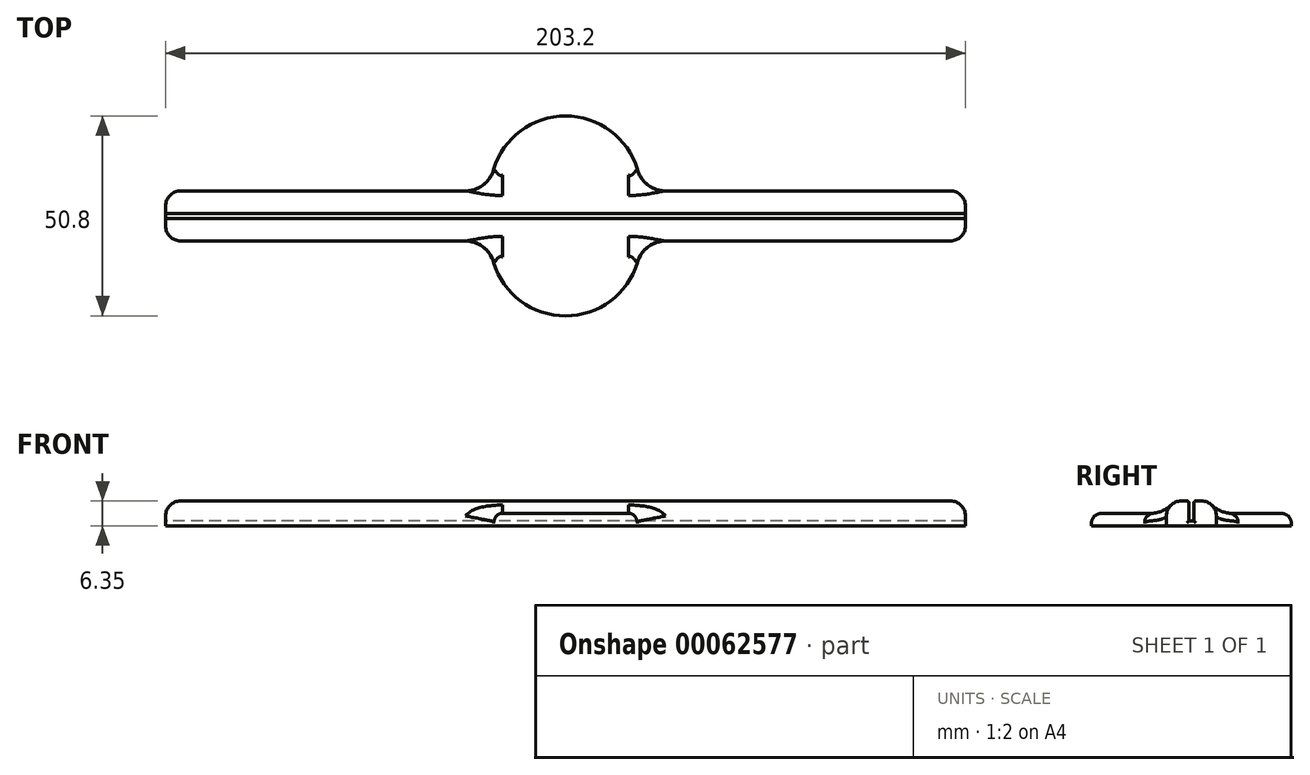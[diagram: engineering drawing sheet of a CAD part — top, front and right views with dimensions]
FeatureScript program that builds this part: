
annotation { "Feature Type Name" : "Feature", "Feature Type Description" : "" }
export const myFeature = defineFeature(function(context is Context, id is Id, definition is map)
    precondition{}
    {
        {
            var Q0;
            Q0=qCreatedBy(makeId("Right.planeOp"),FACE);
            var sketch = newSketch(context, id + "F0", { "sketchPlane" : qUnion([Q0])});
            skPoint(sketch, "E0.visualSharp", {"position": v(5.72, 1.27) * mm});
            skPoint(sketch, "E1.visualSharp", {"position": v(6.99, 1.27) * mm});
            skPoint(sketch, "E2.visualSharp", {"position": v(0, 6.35) * mm});
            skPoint(sketch, "E3.visualSharp", {"position": v(12.7, 6.35) * mm});
            skPoint(sketch, "E4.visualSharp", {"position": v(5.72, 6.35) * mm});
            skPoint(sketch, "E5.visualSharp", {"position": v(6.99, 6.35) * mm});
            skLineSegment(sketch, "E6", {"start": v(12.7, 0) * mm, "end": v(12.7, 6.35) * mm});
            skLineSegment(sketch, "E7", {"start": v(6.99, 6.35) * mm, "end": v(12.7, 6.35) * mm});
            skLineSegment(sketch, "E8", {"start": v(5.72, 6.35) * mm, "end": v(0, 6.35) * mm});
            skLineSegment(sketch, "E9", {"start": v(5.72, 6.35) * mm, "end": v(5.72, 1.27) * mm});
            skLineSegment(sketch, "E10", {"start": v(6.99, 6.35) * mm, "end": v(6.99, 1.27) * mm});
            skLineSegment(sketch, "E11", {"start": v(6.99, 1.27) * mm, "end": v(5.72, 1.27) * mm});
            skLineSegment(sketch, "E12", {"start": v(12.7, 0) * mm, "end": v(0, 0) * mm});
            skLineSegment(sketch, "E13", {"start": v(0, 0) * mm, "end": v(0, 6.35) * mm});
            skSolve(sketch);
        }
        {
            var Q0;
            Q0=makeQuery(id+"F0.imprint","IMPRINT",FACE,{"disambiguationData":[TD([[makeQuery(id+"F0.imprint","IMPRINT",EDGE,{"derivedFrom":sQuery(id+"F0.wireOp",EDGE,"991Wu4Bv-dtFn-WpcZ-A5Xh-EiTTtVhIbmSV")}),1.0]])]});
            var Q1;
            Q1=makeQuery(id+"F0.imprint","IMPRINT",FACE,{"disambiguationData":[TD([[makeQuery(id+"F0.imprint","IMPRINT",EDGE,{"derivedFrom":sQuery(id+"F0.wireOp",EDGE,"E6")}),1.0]])]});
            extrude(context, id + "F1", {"entities" : qUnion([Q0, Q1]), "depth" : 203.2 * mm});
        }
        {
            var Q0;
            Q0=qCreatedBy(makeId("Top.planeOp"),FACE);
            var sketch = newSketch(context, id + "F2", { "sketchPlane" : qUnion([Q0])});
            skArc(sketch, "E14", {"start": v(83.26, 5.16) * mm, "mid": v(101.6, -19.05) * mm, "end": v(119.94, 5.16) * mm});
            skArc(sketch, "E15", {"start": v(119.94, 7.54) * mm, "mid": v(101.6, 31.75) * mm, "end": v(83.26, 7.54) * mm});
            skLineSegment(sketch, "E16", {"start": v(83.26, 5.16) * mm, "end": v(119.94, 5.16) * mm});
            skLineSegment(sketch, "E17", {"start": v(119.94, 7.54) * mm, "end": v(83.26, 7.54) * mm});
            skSolve(sketch);
        }
        {
            var Q0;
            Q0=makeQuery(id+"F2.imprint","IMPRINT",FACE,{"disambiguationData":[TD([[makeQuery(id+"F2.imprint","IMPRINT",EDGE,{"derivedFrom":sQuery(id+"F2.wireOp",EDGE,"E15")}),1.0]])]});
            var Q1;
            Q1=makeQuery(id+"F2.imprint","IMPRINT",FACE,{"disambiguationData":[TD([[makeQuery(id+"F2.imprint","IMPRINT",EDGE,{"derivedFrom":sQuery(id+"F2.wireOp",EDGE,"E14")}),1.0]])]});
            var Q2;
            Q2=makeQuery(id+"F2.imprint","IMPRINT",FACE,{"disambiguationData":[TD([[makeQuery(id+"F2.imprint","IMPRINT",EDGE,{"derivedFrom":sQuery(id+"F2.wireOp",EDGE,"aa7551ad-62cc-4337-8cd2-00c71349cac6")}),1.0]])]});
            var Q3;
            Q3=makeQuery(id+"F2.imprint","IMPRINT",FACE,{"disambiguationData":[TD([[makeQuery(id+"F2.imprint","IMPRINT",EDGE,{"derivedFrom":sQuery(id+"F2.wireOp",EDGE,"730a3766-1bab-460e-ae77-063c695d67be")}),1.0]])]});
            extrude(context, id + "F3", {"entities" : qUnion([Q0, Q1, Q2, Q3]), "operationType" : NewBodyOperationType.ADD, "depth" : 3.17 * mm});
        }
        {
            var Q0;
            Q0=makeQuery(id+"F1.opExtrude","SWEPT_EDGE",EDGE,{"disambiguationData":[OSD([sQuery(id+"F0.wireOp",EDGE,"E6"),sQuery(id+"F0.wireOp",EDGE,"E7")])]});
            var Q1;
            Q1=makeQuery(id+"F1.opExtrude","SWEPT_EDGE",EDGE,{"disambiguationData":[OSD([sQuery(id+"F0.wireOp",EDGE,"E8"),sQuery(id+"F0.wireOp",EDGE,"E13")])]});
            fillet(context, id + "F4", {"entities" : qUnion([Q0, Q1]), "radius" : 3.8 * mm, "tangentPropagation" : true, "allowEdgeOverflow" : false});
        }
        {
            var Q0;
            {var subQ0=sQuery(id+"F0.wireOp",EDGE,"E7");var subQ1=sQuery(id+"F0.wireOp",EDGE,"E6");Q0=makeQuery(id+"F4.opFillet","BLEND_EDGE",EDGE,{"blendedFrom":[makeQuery(id+"F1.opExtrude","SWEPT_EDGE",EDGE,{"disambiguationData":[OSD([subQ1,subQ0])]}),makeQuery(id+"F1.opExtrude","CAP_FACE",FACE,{"disambiguationData":[OSD([subQ1,subQ0,sQuery(id+"F0.wireOp",EDGE,"E8"),sQuery(id+"F0.wireOp",EDGE,"E9"),sQuery(id+"F0.wireOp",EDGE,"E10"),sQuery(id+"F0.wireOp",EDGE,"E11"),sQuery(id+"F0.wireOp",EDGE,"E12"),sQuery(id+"F0.wireOp",EDGE,"E13")])],"isStart":true})],"blendedInto":[makeQuery(id+"F1.opExtrude","CAP_FACE",FACE,{"disambiguationData":[OSD([subQ1,subQ0,sQuery(id+"F0.wireOp",EDGE,"E8"),sQuery(id+"F0.wireOp",EDGE,"E9"),sQuery(id+"F0.wireOp",EDGE,"E10"),sQuery(id+"F0.wireOp",EDGE,"E11"),sQuery(id+"F0.wireOp",EDGE,"E12"),sQuery(id+"F0.wireOp",EDGE,"E13")])],"isStart":true})]});}
            var Q1;
            Q1=makeQuery(id+"F1.opExtrude","CAP_EDGE",EDGE,{"disambiguationData":[OSD([sQuery(id+"F0.wireOp",EDGE,"E7")])],"isStart":true});
            var Q2;
            Q2=makeQuery(id+"F1.opExtrude","CAP_EDGE",EDGE,{"disambiguationData":[OSD([sQuery(id+"F0.wireOp",EDGE,"E8")])],"isStart":true});
            var Q3;
            Q3=makeQuery(id+"F1.opExtrude","CAP_EDGE",EDGE,{"disambiguationData":[OSD([sQuery(id+"F0.wireOp",EDGE,"E6")])],"isStart":false});
            var Q4;
            {var subQ0=sQuery(id+"F0.wireOp",EDGE,"E13");var subQ1=sQuery(id+"F0.wireOp",EDGE,"E8");Q4=makeQuery(id+"F4.opFillet","BLEND_EDGE",EDGE,{"blendedFrom":[makeQuery(id+"F1.opExtrude","SWEPT_EDGE",EDGE,{"disambiguationData":[OSD([subQ1,subQ0])]}),makeQuery(id+"F1.opExtrude","CAP_FACE",FACE,{"disambiguationData":[OSD([sQuery(id+"F0.wireOp",EDGE,"E6"),sQuery(id+"F0.wireOp",EDGE,"E7"),subQ1,sQuery(id+"F0.wireOp",EDGE,"E9"),sQuery(id+"F0.wireOp",EDGE,"E10"),sQuery(id+"F0.wireOp",EDGE,"E11"),sQuery(id+"F0.wireOp",EDGE,"E12"),subQ0])],"isStart":false})],"blendedInto":[makeQuery(id+"F1.opExtrude","CAP_FACE",FACE,{"disambiguationData":[OSD([sQuery(id+"F0.wireOp",EDGE,"E6"),sQuery(id+"F0.wireOp",EDGE,"E7"),subQ1,sQuery(id+"F0.wireOp",EDGE,"E9"),sQuery(id+"F0.wireOp",EDGE,"E10"),sQuery(id+"F0.wireOp",EDGE,"E11"),sQuery(id+"F0.wireOp",EDGE,"E12"),subQ0])],"isStart":false})]});}
            var Q5;
            Q5=makeQuery(id+"F1.opExtrude","CAP_EDGE",EDGE,{"disambiguationData":[OSD([sQuery(id+"F0.wireOp",EDGE,"E6")])],"isStart":true});
            var Q6;
            {var subQ0=sQuery(id+"F0.wireOp",EDGE,"E13");var subQ1=sQuery(id+"F0.wireOp",EDGE,"E8");Q6=makeQuery(id+"F4.opFillet","BLEND_EDGE",EDGE,{"blendedFrom":[makeQuery(id+"F1.opExtrude","SWEPT_EDGE",EDGE,{"disambiguationData":[OSD([subQ1,subQ0])]}),makeQuery(id+"F1.opExtrude","CAP_FACE",FACE,{"disambiguationData":[OSD([sQuery(id+"F0.wireOp",EDGE,"E6"),sQuery(id+"F0.wireOp",EDGE,"E7"),subQ1,sQuery(id+"F0.wireOp",EDGE,"E9"),sQuery(id+"F0.wireOp",EDGE,"E10"),sQuery(id+"F0.wireOp",EDGE,"E11"),sQuery(id+"F0.wireOp",EDGE,"E12"),subQ0])],"isStart":true})],"blendedInto":[makeQuery(id+"F1.opExtrude","CAP_FACE",FACE,{"disambiguationData":[OSD([sQuery(id+"F0.wireOp",EDGE,"E6"),sQuery(id+"F0.wireOp",EDGE,"E7"),subQ1,sQuery(id+"F0.wireOp",EDGE,"E9"),sQuery(id+"F0.wireOp",EDGE,"E10"),sQuery(id+"F0.wireOp",EDGE,"E11"),sQuery(id+"F0.wireOp",EDGE,"E12"),subQ0])],"isStart":true})]});}
            var Q7;
            Q7=makeQuery(id+"F1.opExtrude","CAP_EDGE",EDGE,{"disambiguationData":[OSD([sQuery(id+"F0.wireOp",EDGE,"E13")])],"isStart":true});
            var Q8;
            {var subQ0=sQuery(id+"F0.wireOp",EDGE,"E7");var subQ1=sQuery(id+"F0.wireOp",EDGE,"E6");Q8=makeQuery(id+"F4.opFillet","BLEND_EDGE",EDGE,{"blendedFrom":[makeQuery(id+"F1.opExtrude","SWEPT_EDGE",EDGE,{"disambiguationData":[OSD([subQ1,subQ0])]}),makeQuery(id+"F1.opExtrude","CAP_FACE",FACE,{"disambiguationData":[OSD([subQ1,subQ0,sQuery(id+"F0.wireOp",EDGE,"E8"),sQuery(id+"F0.wireOp",EDGE,"E9"),sQuery(id+"F0.wireOp",EDGE,"E10"),sQuery(id+"F0.wireOp",EDGE,"E11"),sQuery(id+"F0.wireOp",EDGE,"E12"),sQuery(id+"F0.wireOp",EDGE,"E13")])],"isStart":false})],"blendedInto":[makeQuery(id+"F1.opExtrude","CAP_FACE",FACE,{"disambiguationData":[OSD([subQ1,subQ0,sQuery(id+"F0.wireOp",EDGE,"E8"),sQuery(id+"F0.wireOp",EDGE,"E9"),sQuery(id+"F0.wireOp",EDGE,"E10"),sQuery(id+"F0.wireOp",EDGE,"E11"),sQuery(id+"F0.wireOp",EDGE,"E12"),sQuery(id+"F0.wireOp",EDGE,"E13")])],"isStart":false})]});}
            var Q9;
            Q9=makeQuery(id+"F1.opExtrude","CAP_EDGE",EDGE,{"disambiguationData":[OSD([sQuery(id+"F0.wireOp",EDGE,"E7")])],"isStart":false});
            var Q10;
            Q10=makeQuery(id+"F1.opExtrude","CAP_EDGE",EDGE,{"disambiguationData":[OSD([sQuery(id+"F0.wireOp",EDGE,"E8")])],"isStart":false});
            var Q11;
            Q11=makeQuery(id+"F1.opExtrude","CAP_EDGE",EDGE,{"disambiguationData":[OSD([sQuery(id+"F0.wireOp",EDGE,"E13")])],"isStart":false});
            fillet(context, id + "F5", {"entities" : qUnion([Q0, Q1, Q2, Q3, Q4, Q5, Q6, Q7, Q8, Q9, Q10, Q11]), "radius" : 3.8 * mm, "tangentPropagation" : true, "allowEdgeOverflow" : false});
        }
        {
            var Q0;
            Q0=makeQuery(id+"F3.opExtrude","CAP_EDGE",EDGE,{"disambiguationData":[OSD([sQuery(id+"F2.wireOp",EDGE,"aa7551ad-62cc-4337-8cd2-00c71349cac6")])],"isStart":false});
            var Q1;
            Q1=makeQuery(id+"F3.opExtrude","CAP_EDGE",EDGE,{"disambiguationData":[OSD([sQuery(id+"F2.wireOp",EDGE,"730a3766-1bab-460e-ae77-063c695d67be")])],"isStart":false});
            var Q2;
            Q2=makeQuery(id+"F3.opExtrude","CAP_EDGE",EDGE,{"disambiguationData":[OSD([sQuery(id+"F2.wireOp",EDGE,"E14")])],"isStart":false});
            var Q3;
            Q3=makeQuery(id+"F3.opExtrude","CAP_EDGE",EDGE,{"disambiguationData":[OSD([sQuery(id+"F2.wireOp",EDGE,"E15")])],"isStart":false});
            fillet(context, id + "F6", {"entities" : qUnion([Q0, Q1, Q2, Q3]), "radius" : 2.54 * mm, "tangentPropagation" : true, "allowEdgeOverflow" : false});
        }
        {
            var Q0;
            Q0=makeQuery(id+"F4.opFillet","BLEND_EDGE",EDGE,{"blendedFrom":[makeQuery(id+"F1.opExtrude","SWEPT_EDGE",EDGE,{"disambiguationData":[OSD([sQuery(id+"F0.wireOp",EDGE,"E8"),sQuery(id+"F0.wireOp",EDGE,"E13")])]}),makeQuery(id+"F3.opExtrude","CAP_FACE",FACE,{"disambiguationData":[OSD([sQuery(id+"F2.wireOp",EDGE,"E14"),sQuery(id+"F2.wireOp",EDGE,"E16")])],"isStart":false})],"blendedInto":[makeQuery(id+"F3.opExtrude","CAP_FACE",FACE,{"disambiguationData":[OSD([sQuery(id+"F2.wireOp",EDGE,"E14"),sQuery(id+"F2.wireOp",EDGE,"E16")])],"isStart":false})]});
            var Q1;
            Q1=makeQuery(id+"F4.opFillet","BLEND_EDGE",EDGE,{"blendedFrom":[makeQuery(id+"F1.opExtrude","SWEPT_EDGE",EDGE,{"disambiguationData":[OSD([sQuery(id+"F0.wireOp",EDGE,"E6"),sQuery(id+"F0.wireOp",EDGE,"E7")])]}),makeQuery(id+"F3.opExtrude","CAP_FACE",FACE,{"disambiguationData":[OSD([sQuery(id+"F2.wireOp",EDGE,"E15"),sQuery(id+"F2.wireOp",EDGE,"E17")])],"isStart":false})],"blendedInto":[makeQuery(id+"F3.opExtrude","CAP_FACE",FACE,{"disambiguationData":[OSD([sQuery(id+"F2.wireOp",EDGE,"E15"),sQuery(id+"F2.wireOp",EDGE,"E17")])],"isStart":false})]});
            var Q2;
            Q2=makeQuery(id+"F4.opFillet","BLEND_EDGE",EDGE,{"blendedFrom":[makeQuery(id+"F1.opExtrude","SWEPT_EDGE",EDGE,{"disambiguationData":[OSD([sQuery(id+"F0.wireOp",EDGE,"E6"),sQuery(id+"F0.wireOp",EDGE,"E7")])]}),makeQuery(id+"F3.opExtrude","CAP_FACE",FACE,{"disambiguationData":[OSD([sQuery(id+"F2.wireOp",EDGE,"730a3766-1bab-460e-ae77-063c695d67be"),sQuery(id+"F2.wireOp",EDGE,"qgNIvyve-4aoE-YkwQ-8RIo-ycNqhRU7BuWn")])],"isStart":false})],"blendedInto":[makeQuery(id+"F3.opExtrude","CAP_FACE",FACE,{"disambiguationData":[OSD([sQuery(id+"F2.wireOp",EDGE,"730a3766-1bab-460e-ae77-063c695d67be"),sQuery(id+"F2.wireOp",EDGE,"qgNIvyve-4aoE-YkwQ-8RIo-ycNqhRU7BuWn")])],"isStart":false})]});
            var Q3;
            Q3=makeQuery(id+"F4.opFillet","BLEND_EDGE",EDGE,{"blendedFrom":[makeQuery(id+"F1.opExtrude","SWEPT_EDGE",EDGE,{"disambiguationData":[OSD([sQuery(id+"F0.wireOp",EDGE,"E8"),sQuery(id+"F0.wireOp",EDGE,"E13")])]}),makeQuery(id+"F3.opExtrude","CAP_FACE",FACE,{"disambiguationData":[OSD([sQuery(id+"F2.wireOp",EDGE,"aa7551ad-62cc-4337-8cd2-00c71349cac6"),sQuery(id+"F2.wireOp",EDGE,"Je3wa9sZ-6DaJ-dVhN-PLyj-Axz1OOrvABwR")])],"isStart":false})],"blendedInto":[makeQuery(id+"F3.opExtrude","CAP_FACE",FACE,{"disambiguationData":[OSD([sQuery(id+"F2.wireOp",EDGE,"aa7551ad-62cc-4337-8cd2-00c71349cac6"),sQuery(id+"F2.wireOp",EDGE,"Je3wa9sZ-6DaJ-dVhN-PLyj-Axz1OOrvABwR")])],"isStart":false})]});
            fillet(context, id + "F7", {"entities" : qUnion([Q0, Q1, Q2, Q3]), "radius" : 7.62 * mm, "tangentPropagation" : true, "allowEdgeOverflow" : false});
        }
        {
            var Q0;
            Q0=makeQuery(id+"F1.opExtrude","CAP_EDGE",EDGE,{"disambiguationData":[OSD([sQuery(id+"F0.wireOp",EDGE,"E10")])],"isStart":true});
            var Q1;
            Q1=makeQuery(id+"F1.opExtrude","CAP_EDGE",EDGE,{"disambiguationData":[OSD([sQuery(id+"F0.wireOp",EDGE,"E9")])],"isStart":true});
            var Q2;
            Q2=makeQuery(id+"F1.opExtrude","SWEPT_EDGE",EDGE,{"disambiguationData":[OSD([sQuery(id+"F0.wireOp",EDGE,"E7"),sQuery(id+"F0.wireOp",EDGE,"E10")])]});
            var Q3;
            Q3=makeQuery(id+"F1.opExtrude","SWEPT_EDGE",EDGE,{"disambiguationData":[OSD([sQuery(id+"F0.wireOp",EDGE,"E8"),sQuery(id+"F0.wireOp",EDGE,"E9")])]});
            var Q4;
            Q4=makeQuery(id+"F5.opFillet","BLEND_EDGE",EDGE,{"blendedFrom":[makeQuery(id+"F1.opExtrude","CAP_EDGE",EDGE,{"disambiguationData":[OSD([sQuery(id+"F0.wireOp",EDGE,"E8")])],"isStart":true}),makeQuery(id+"F1.opExtrude","SWEPT_FACE",FACE,{"disambiguationData":[OSD([sQuery(id+"F0.wireOp",EDGE,"E9")])]})],"blendedInto":[makeQuery(id+"F1.opExtrude","SWEPT_FACE",FACE,{"disambiguationData":[OSD([sQuery(id+"F0.wireOp",EDGE,"E9")])]})]});
            var Q5;
            Q5=makeQuery(id+"F5.opFillet","BLEND_EDGE",EDGE,{"blendedFrom":[makeQuery(id+"F1.opExtrude","CAP_EDGE",EDGE,{"disambiguationData":[OSD([sQuery(id+"F0.wireOp",EDGE,"E7")])],"isStart":true}),makeQuery(id+"F1.opExtrude","SWEPT_FACE",FACE,{"disambiguationData":[OSD([sQuery(id+"F0.wireOp",EDGE,"E10")])]})],"blendedInto":[makeQuery(id+"F1.opExtrude","SWEPT_FACE",FACE,{"disambiguationData":[OSD([sQuery(id+"F0.wireOp",EDGE,"E10")])]})]});
            var Q6;
            Q6=makeQuery(id+"F5.opFillet","BLEND_EDGE",EDGE,{"blendedFrom":[makeQuery(id+"F1.opExtrude","CAP_EDGE",EDGE,{"disambiguationData":[OSD([sQuery(id+"F0.wireOp",EDGE,"E7")])],"isStart":false}),makeQuery(id+"F1.opExtrude","SWEPT_FACE",FACE,{"disambiguationData":[OSD([sQuery(id+"F0.wireOp",EDGE,"E10")])]})],"blendedInto":[makeQuery(id+"F1.opExtrude","SWEPT_FACE",FACE,{"disambiguationData":[OSD([sQuery(id+"F0.wireOp",EDGE,"E10")])]})]});
            var Q7;
            Q7=makeQuery(id+"F1.opExtrude","CAP_EDGE",EDGE,{"disambiguationData":[OSD([sQuery(id+"F0.wireOp",EDGE,"E10")])],"isStart":false});
            var Q8;
            Q8=makeQuery(id+"F1.opExtrude","CAP_EDGE",EDGE,{"disambiguationData":[OSD([sQuery(id+"F0.wireOp",EDGE,"E9")])],"isStart":false});
            var Q9;
            Q9=makeQuery(id+"F5.opFillet","BLEND_EDGE",EDGE,{"blendedFrom":[makeQuery(id+"F1.opExtrude","CAP_EDGE",EDGE,{"disambiguationData":[OSD([sQuery(id+"F0.wireOp",EDGE,"E8")])],"isStart":false}),makeQuery(id+"F1.opExtrude","SWEPT_FACE",FACE,{"disambiguationData":[OSD([sQuery(id+"F0.wireOp",EDGE,"E9")])]})],"blendedInto":[makeQuery(id+"F1.opExtrude","SWEPT_FACE",FACE,{"disambiguationData":[OSD([sQuery(id+"F0.wireOp",EDGE,"E9")])]})]});
            var Q10;
            Q10=makeQuery(id+"F1.opExtrude","CAP_EDGE",EDGE,{"disambiguationData":[OSD([sQuery(id+"F0.wireOp",EDGE,"E11")])],"isStart":false});
            var Q11;
            Q11=makeQuery(id+"F1.opExtrude","CAP_EDGE",EDGE,{"disambiguationData":[OSD([sQuery(id+"F0.wireOp",EDGE,"E11")])],"isStart":true});
            fillet(context, id + "F8", {"entities" : qUnion([Q0, Q1, Q2, Q3, Q4, Q5, Q6, Q7, Q8, Q9, Q10, Q11]), "radius" : 0.5 * mm, "tangentPropagation" : true, "allowEdgeOverflow" : false});
        }
    });
